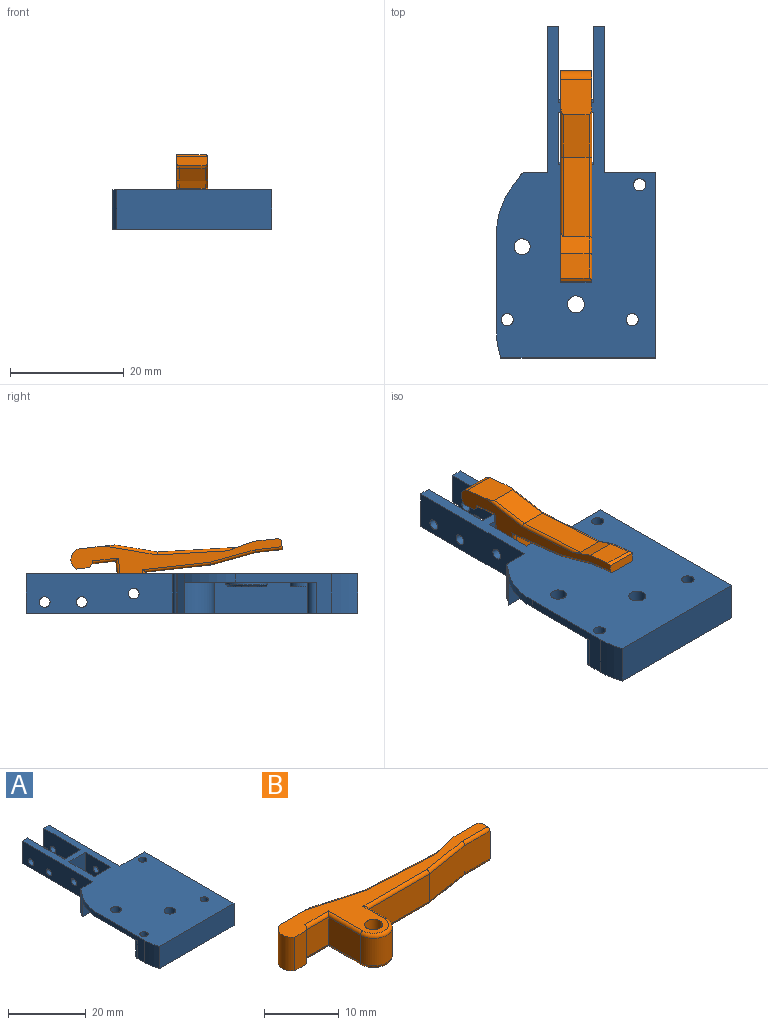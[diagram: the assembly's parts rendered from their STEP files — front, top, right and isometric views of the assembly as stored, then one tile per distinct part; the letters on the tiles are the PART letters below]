
ASSEMBLY  parts=2 mates=1
PART A: 66 faces, bbox 28x58.4x7 mm
  f0: plane 5.7x1.95mm, normal (0,1,0), area 11.1mm2, adj f1,f2,f36,f56
  f1: plane 25.8x7mm, normal (1,0,0), area 164.8mm2, adj f0,f3,f4,f18,f35,f36,f53,f54
  f2: plane 13.5x7mm, normal (-1,0,0), area 78.2mm2, adj f0,f3,f4,f19,f35,f36,f53,f54
  f3: plane 3.34x1.95mm, normal (0,0,-1), area 6.5mm2, adj f1,f2,f59,f63
  f4: plane 3.96x1.95mm, normal (0,0,-1), area 7.7mm2, adj f1,f2,f57,f60
  f5: plane 5.5x1.29mm, normal (1,0,0), area 7.1mm2, adj f35,f39,f41,f42
  f6: plane 5.5x0.8mm, normal (0,1,0), area 4.4mm2, adj f35,f39,f40,f42
  f7: plane 5.5x3.25mm, normal (0,1,0), area 17.8mm2, adj f8,f28,f35,f39
  f8: plane 5.5x4.2mm, normal (-1,0,0), area 23.1mm2, adj f7,f9,f35,f39
  f9: plane 5.5x3.25mm, normal (0,-1,0), area 17.8mm2, adj f8,f29,f35,f39
  f10: plane 7x6mm, normal (0,-1,0), area 42mm2, adj f11,f30,f35,f36
  f11: plane 9.3x7mm, normal (-1,0,0), area 58.9mm2, adj f10,f12,f35,f36,f55,f64
  f12: plane 6.5x6mm, normal (0,1,0), area 39mm2, adj f11,f30,f35,f64
  f13: cylinder r=11.2mm len=5.5mm, axis (0,0,1), area 14.1mm2, adj f33,f35,f39,f41
  f14: plane 17x7mm, normal (-1,0,0), area 40.4mm2, adj f15,f35,f36,f38,f39,f40
  f15: cylinder r=14mm len=7mm, axis (0,0,1), area 33mm2, adj f14,f16,f35,f36
  f16: plane 27.22x7mm, normal (0,-1,0), area 190.5mm2, adj f15,f17,f35,f36
  f17: plane 32.62x7mm, normal (1,0,0), area 228.4mm2, adj f16,f18,f35,f36
  f18: plane 9.05x7mm, normal (0,1,0), area 63.3mm2, adj f1,f17,f35,f36
  f19: plane 6.5x6mm, normal (0,1,0), area 39mm2, adj f2,f20,f35,f65
  f20: plane 13.5x7mm, normal (1,0,0), area 85.5mm2, adj f19,f21,f35,f36,f51,f52,f65
  f21: plane 7x1.95mm, normal (0,1,0), area 13.7mm2, adj f20,f22,f35,f36
  f22: plane 25.8x7mm, normal (-1,0,0), area 172.1mm2, adj f21,f23,f35,f36,f50,f51,f52
  f23: plane 7x3.99mm, normal (0,1,0), area 27.9mm2, adj f22,f35,f36,f46
  f24: plane 7x0.18mm, normal (-0.95,0.33,0), area 1.3mm2, adj f25,f35,f36,f46
  f25: plane 7x1.3mm, normal (-0.78,0.62,0), area 11.6mm2, adj f24,f26,f35,f36,f38
  f26: plane 17.02x5.5mm, normal (0,-1,0), area 93.6mm2, adj f25,f27,f35,f39
  f27: cylinder r=5.16mm len=5.5mm, axis (0,0,1), area 44.6mm2, adj f26,f28,f35,f39
  f28: plane 16.49x5.5mm, normal (-1,0,0), area 90.7mm2, adj f7,f27,f35,f39
  f29: cylinder r=11.2mm len=5.5mm, axis (0,0,1), area 14.1mm2, adj f9,f33,f35,f39
  f30: plane 9.3x7mm, normal (1,0,0), area 58.9mm2, adj f10,f12,f35,f36,f50,f64
  f31: cylinder r=1.07mm len=7mm, axis (0,0,1), area 47.3mm2, adj f35,f36
  f32: cylinder r=1.07mm len=7mm, axis (0,0,1), area 47.3mm2, adj f35,f36
  f33: plane 21.81x5.5mm, normal (0,1,0), area 120mm2, adj f13,f29,f35,f39
  f34: cylinder r=1.07mm len=7mm, axis (0,0,1), area 47.3mm2, adj f35,f36
  f35: plane 58.42x28mm, normal (0,0,-1), area 333.7mm2, adj f1,f2,f5,f6,f7,f8,f9,f10
  f36: plane 58.42x28mm, normal (0,0,1), area 990.1mm2, adj f0,f1,f2,f10,f11,f14,f15,f16
  f37: cylinder r=1.4mm len=2.8mm, axis (0,0,1), area 20.2mm2, adj f36,f44
  f38: cylinder r=14mm len=8.85mm, axis (0,0,1), area 14.3mm2, adj f14,f25,f36,f39
  f39: plane 28.39x25.2mm, normal (0,0,-1), area 587.8mm2, adj f5,f6,f7,f8,f9,f13,f14,f26
  f40: cylinder r=1.5mm len=5.5mm, axis (0,0,1), area 13mm2, adj f6,f14,f35,f39
  f41: cylinder r=1.5mm len=5.5mm, axis (0,0,1), area 10.2mm2, adj f5,f13,f35,f39
  f42: cylinder r=1.5mm len=5.5mm, axis (0,0,1), area 13mm2, adj f5,f6,f35,f39
  f43: cylinder r=3.7mm len=7.4mm, axis (0,0,1), area 11.6mm2, adj f39,f45
  f44: plane 6.8x6.8mm, normal (0,0,-1), area 30.2mm2, adj f37,f45
  f45: cone r=3.7mm half-angle=45deg, axis (0,0,1), area 9.5mm2, adj f43,f44
  f46: cylinder r=1mm len=7mm, axis (0,0,1), area 8.7mm2, adj f23,f24,f35,f36
  f47: cylinder r=2.5mm len=5mm, axis (0,0,1), area 12.6mm2, adj f39,f49
  f48: cylinder r=1.5mm len=3mm, axis (0,0,1), area 21.7mm2, adj f36,f49
  f49: plane 5x5mm, normal (0,0,-1), area 12.6mm2, adj f47,f48
  f50: cylinder r=0.95mm len=1.95mm, axis (-1,0,0), area 11.6mm2, adj f22,f30
  f51: cylinder r=0.95mm len=1.95mm, axis (-1,0,0), area 11.6mm2, adj f20,f22
  f52: cylinder r=0.95mm len=1.95mm, axis (-1,0,0), area 11.6mm2, adj f20,f22
  f53: cylinder r=0.95mm len=1.95mm, axis (-1,0,0), area 11.6mm2, adj f1,f2
  f54: cylinder r=0.95mm len=1.95mm, axis (-1,0,0), area 11.6mm2, adj f1,f2
  f55: cylinder r=0.95mm len=1.95mm, axis (-1,0,0), area 11.6mm2, adj f1,f11
  f56: plane 1.95x1.5mm, normal (0,0,-1), area 2.9mm2, adj f0,f1,f2,f57
  f57: plane 1.95x1.3mm, normal (0,1,0), area 2.5mm2, adj f1,f2,f4,f56
  f58: plane 2.5x1.95mm, normal (0,0,-1), area 4.9mm2, adj f1,f2,f59,f60
  f59: plane 1.95x1.3mm, normal (0,1,0), area 2.5mm2, adj f1,f2,f3,f58
  f60: plane 1.95x1.3mm, normal (0,-1,0), area 2.5mm2, adj f1,f2,f4,f58
  f61: plane 1.95x1.6mm, normal (0,0,-1), area 3.1mm2, adj f1,f2,f62,f63
  f62: plane 1.95x1.3mm, normal (0,1,0), area 2.5mm2, adj f1,f2,f35,f61
  f63: plane 1.95x1.3mm, normal (0,-1,0), area 2.5mm2, adj f1,f2,f3,f61
  f64: plane 6x0.5mm, normal (0,0.71,0.71), area 4.2mm2, adj f11,f12,f30,f36
  f65: plane 6x0.5mm, normal (0,0.71,0.71), area 4.2mm2, adj f2,f19,f20,f36
PART B: 40 faces, bbox 37.2x12.1x5.5 mm
  f0: plane 6.26x5.5mm, normal (0,1,0), area 34mm2, adj f1,f17,f18,f19,f30,f35
  f1: cylinder r=1.93mm len=5.5mm, axis (0,0,-1), area 25.3mm2, adj f0,f2,f18,f19
  f2: plane 5.5x2.26mm, normal (0,-1,0), area 12.4mm2, adj f1,f3,f18,f19
  f3: cylinder r=1.93mm len=5.5mm, axis (0,0,-1), area 4.7mm2, adj f2,f4,f18,f19,f20,f24
  f4: plane 4.5x4.24mm, normal (0,-1,0), area 19.1mm2, adj f3,f5,f20,f24
  f5: plane 6.01x4.5mm, normal (-1,0,0), area 27mm2, adj f4,f6,f21,f25
  f6: cylinder r=2.5mm len=5mm, axis (0,0,-1), area 35.3mm2, adj f5,f7,f22,f26
  f7: plane 4.5x3.5mm, normal (1,0,0), area 15.7mm2, adj f6,f8,f23,f27
  f8: plane 11.6x4.5mm, normal (0,-1,0), area 52.2mm2, adj f7,f9,f32,f37
  f9: plane 8.02x4.5mm, normal (0.16,-0.99,0), area 36.6mm2, adj f8,f10,f33,f38
  f10: plane 4.74x4.5mm, normal (0,-1,0), area 21.3mm2, adj f9,f11,f34,f39
  f11: plane 5.5x1.64mm, normal (1,0,0), area 8.9mm2, adj f10,f12,f18,f19,f28,f34,f39
  f12: plane 5.48x0.5mm, normal (0.58,0.81,0), area 3.3mm2, adj f11,f13,f18,f28
  f13: plane 5x4.32mm, normal (0,1,0), area 21.6mm2, adj f12,f14,f18,f28
  f14: plane 5x4.77mm, normal (-0.24,0.97,0), area 16mm2, adj f13,f15,f18,f29,f36
  f15: plane 14.03x4.5mm, normal (0.05,1,0), area 63.2mm2, adj f14,f17,f31,f36
  f16: cylinder r=1.2mm len=5.5mm, axis (0,0,-1), area 41.5mm2, adj f18,f19
  f17: plane 7.31x4.5mm, normal (0.27,0.96,0), area 34.2mm2, adj f0,f15,f30,f35
  f18: plane 37.19x10.87mm, normal (0,0,1), area 99mm2, adj f0,f1,f2,f3,f11,f12,f13,f14
  f19: plane 37.19x10.87mm, normal (0,0,-1), area 94.7mm2, adj f0,f1,f2,f3,f11,f16,f20,f21
  f20: cylinder r=0.5mm len=4.74mm, axis (1,0,0), area 3.4mm2, adj f3,f4,f19,f21
  f21: cylinder r=0.5mm len=6.51mm, axis (0,-1,0), area 4.9mm2, adj f5,f19,f20,f22
  f22: torus R=2mm, axis (0,0,1), area 5.7mm2, adj f6,f19,f21,f23
  f23: cylinder r=0.5mm len=4mm, axis (0,1,0), area 2.9mm2, adj f7,f19,f22,f32
  f24: cylinder r=0.5mm len=4.74mm, axis (-1,0,0), area 3.4mm2, adj f3,f4,f18,f25
  f25: cylinder r=0.5mm len=6.51mm, axis (0,1,0), area 4.9mm2, adj f5,f18,f24,f26
  f26: torus R=2mm, axis (0,0,1), area 5.7mm2, adj f6,f18,f25,f27
  f27: cylinder r=0.5mm len=4mm, axis (0,-1,0), area 2.9mm2, adj f7,f18,f26,f37
  f28: cylinder r=0.5mm len=4.82mm, axis (-1,0,0), area 3.6mm2, adj f11,f12,f13,f19,f29
  f29: cylinder r=0.5mm len=3.26mm, axis (-0.97,-0.24,0), area 2.5mm2, adj f14,f19,f28,f31
  f30: cylinder r=0.5mm len=9.2mm, axis (-0.96,0.27,0), area 6.5mm2, adj f0,f17,f19,f31
  f31: cylinder r=0.5mm len=14.18mm, axis (-1,0.05,0), area 11.1mm2, adj f15,f19,f29,f30
  f32: cylinder r=0.5mm len=12.1mm, axis (1,0,0), area 9.2mm2, adj f8,f19,f23,f33
  f33: cylinder r=0.5mm len=8.14mm, axis (0.99,0.16,0), area 6.4mm2, adj f9,f19,f32,f34
  f34: cylinder r=0.5mm len=4.78mm, axis (1,0,0), area 3.7mm2, adj f10,f11,f19,f33
  f35: cylinder r=0.5mm len=9.2mm, axis (0.96,-0.27,0), area 6.5mm2, adj f0,f17,f18,f36
  f36: cylinder r=0.5mm len=14.11mm, axis (1,-0.05,0), area 10.6mm2, adj f14,f15,f18,f35
  f37: cylinder r=0.5mm len=12.1mm, axis (-1,0,0), area 9.2mm2, adj f8,f18,f27,f38
  f38: cylinder r=0.5mm len=8.14mm, axis (-0.99,-0.16,0), area 6.4mm2, adj f9,f18,f37,f39
  f39: cylinder r=0.5mm len=4.78mm, axis (-1,0,0), area 3.7mm2, adj f10,f11,f18,f38
PLACE A at identity fixed
PLACE B rot(axis=(0.55,-0.62,-0.55),116.4deg) t=(2.8,34.85,-3.5)mm
MATE cylindrical A.f50 <-> B.f16  axis (-1,0,0) through (3,34.85,-3.5)mm
